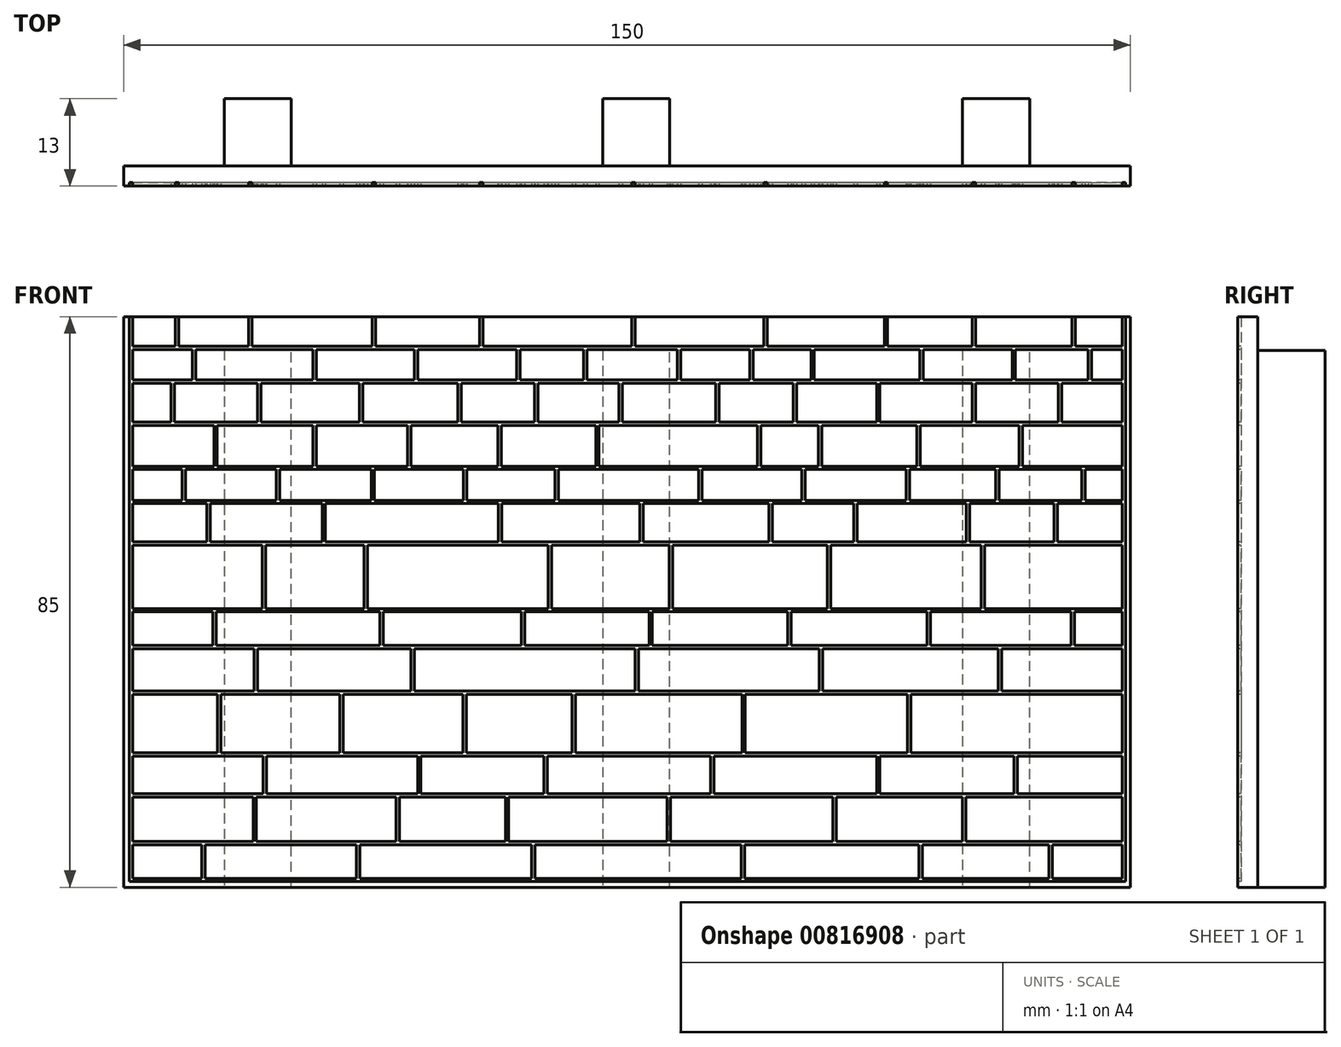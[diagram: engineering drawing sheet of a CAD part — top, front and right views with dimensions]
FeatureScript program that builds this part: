
annotation { "Feature Type Name" : "Feature", "Feature Type Description" : "" }
export const myFeature = defineFeature(function(context is Context, id is Id, definition is map)
    precondition{}
    {
        {
            var Q0;
            Q0=qCreatedBy(makeId("Front.planeOp"),FACE);
            var sketch = newSketch(context, id + "F0", { "sketchPlane" : qUnion([Q0])});
            skLineSegment(sketch, "E0.bottom", {"start": v(-65.97, 73.81) * mm, "end": v(-58.47, 73.81) * mm});
            skLineSegment(sketch, "E0.top", {"start": v(-65.97, -46.19) * mm, "end": v(84.03, -46.19) * mm});
            skLineSegment(sketch, "E0.left", {"start": v(-65.97, 73.81) * mm, "end": v(-65.97, -46.19) * mm});
            skLineSegment(sketch, "E0.right", {"start": v(84.03, 73.81) * mm, "end": v(84.03, -46.19) * mm});
            skLineSegment(sketch, "E1", {"start": v(-58.47, 73.81) * mm, "end": v(-58.47, 43.81) * mm});
            skLineSegment(sketch, "E2", {"start": v(-58.47, 43.81) * mm, "end": v(-43.47, 43.81) * mm});
            skLineSegment(sketch, "E3", {"start": v(-43.47, 43.81) * mm, "end": v(-43.47, 73.81) * mm});
            skLineSegment(sketch, "E4", {"start": v(-43.47, 73.81) * mm, "end": v(-28.47, 73.81) * mm});
            skLineSegment(sketch, "E5", {"start": v(1.53, 73.81) * mm, "end": v(1.53, 43.81) * mm});
            skLineSegment(sketch, "E6", {"start": v(1.53, 43.81) * mm, "end": v(16.53, 43.81) * mm});
            skLineSegment(sketch, "E7", {"start": v(16.53, 43.81) * mm, "end": v(16.53, 73.81) * mm});
            skLineSegment(sketch, "E8", {"start": v(16.53, 73.81) * mm, "end": v(31.53, 73.81) * mm});
            skLineSegment(sketch, "E9", {"start": v(61.53, 73.81) * mm, "end": v(61.53, 43.81) * mm});
            skLineSegment(sketch, "E10", {"start": v(61.53, 43.81) * mm, "end": v(76.53, 43.81) * mm});
            skLineSegment(sketch, "E11", {"start": v(76.53, 43.81) * mm, "end": v(76.53, 73.81) * mm});
            skLineSegment(sketch, "E12.trimOffspring", {"start": v(76.53, 73.81) * mm, "end": v(84.03, 73.81) * mm});
            skLineSegment(sketch, "E13", {"start": v(-28.47, 73.81) * mm, "end": v(-28.47, 43.81) * mm});
            skLineSegment(sketch, "E14", {"start": v(-28.47, 43.81) * mm, "end": v(-13.47, 43.81) * mm});
            skLineSegment(sketch, "E15", {"start": v(-13.47, 43.81) * mm, "end": v(-13.47, 73.81) * mm});
            skLineSegment(sketch, "E16", {"start": v(31.53, 73.81) * mm, "end": v(31.53, 43.81) * mm});
            skLineSegment(sketch, "E17", {"start": v(31.53, 43.81) * mm, "end": v(46.53, 43.81) * mm});
            skLineSegment(sketch, "E18", {"start": v(46.53, 43.81) * mm, "end": v(46.53, 73.81) * mm});
            skLineSegment(sketch, "E19.trimOffspring", {"start": v(-13.47, 73.81) * mm, "end": v(1.53, 73.81) * mm});
            skLineSegment(sketch, "E20.trimOffspring", {"start": v(46.53, 73.81) * mm, "end": v(61.53, 73.81) * mm});
            skSolve(sketch);
        }
        {
            var Q0;
            Q0=qSketchRegion(id+"F0",true);
            extrude(context, id + "F1", {"entities" : qUnion([Q0]), "depth" : 3 * mm, "offsetDistance" : 25 * mm});
        }
        {
            var Q0;
            Q0=makeQuery(id+"F1.opExtrude","CAP_FACE",FACE,{"disambiguationData":[OSD([sQuery(id+"F0.wireOp",EDGE,"E0.bottom"),sQuery(id+"F0.wireOp",EDGE,"E0.top"),sQuery(id+"F0.wireOp",EDGE,"E0.left"),sQuery(id+"F0.wireOp",EDGE,"E0.right"),sQuery(id+"F0.wireOp",EDGE,"E1"),sQuery(id+"F0.wireOp",EDGE,"E2"),sQuery(id+"F0.wireOp",EDGE,"E3"),sQuery(id+"F0.wireOp",EDGE,"E5"),sQuery(id+"F0.wireOp",EDGE,"E6"),sQuery(id+"F0.wireOp",EDGE,"E7"),sQuery(id+"F0.wireOp",EDGE,"E9"),sQuery(id+"F0.wireOp",EDGE,"E10"),sQuery(id+"F0.wireOp",EDGE,"E11"),sQuery(id+"F0.wireOp",EDGE,"E4"),sQuery(id+"F0.wireOp",EDGE,"E8"),sQuery(id+"F0.wireOp",EDGE,"E12.trimOffspring"),sQuery(id+"F0.wireOp",EDGE,"E13"),sQuery(id+"F0.wireOp",EDGE,"E14"),sQuery(id+"F0.wireOp",EDGE,"E15"),sQuery(id+"F0.wireOp",EDGE,"E16"),sQuery(id+"F0.wireOp",EDGE,"E17"),sQuery(id+"F0.wireOp",EDGE,"E18"),sQuery(id+"F0.wireOp",EDGE,"E19.trimOffspring"),sQuery(id+"F0.wireOp",EDGE,"E20.trimOffspring")])],"isStart":false});
            var sketch = newSketch(context, id + "F2", { "sketchPlane" : qUnion([Q0])});
            skLineSegment(sketch, "E21", {"start": v(-64.64, -39.38) * mm, "end": v(-46.68, -39.38) * mm});
            skLineSegment(sketch, "E22", {"start": v(83.31, -39.38) * mm, "end": v(83.31, -45.36) * mm});
            skLineSegment(sketch, "E23", {"start": v(83.31, -45.36) * mm, "end": v(-65.14, -45.36) * mm});
            skLineSegment(sketch, "E24", {"start": v(-65.14, -45.36) * mm, "end": v(-65.14, -39.38) * mm});
            skLineSegment(sketch, "E25.0", {"start": v(-64.64, -39.88) * mm, "end": v(-54.3, -39.88) * mm});
            skLineSegment(sketch, "E26.0", {"start": v(82.81, -44.86) * mm, "end": v(72.42, -44.86) * mm});
            skLineSegment(sketch, "E27.0", {"start": v(-64.64, -44.86) * mm, "end": v(-64.64, -39.88) * mm});
            skLineSegment(sketch, "E28.0", {"start": v(82.81, -39.88) * mm, "end": v(82.81, -44.86) * mm});
            skLineSegment(sketch, "E29", {"start": v(-65.14, -39.38) * mm, "end": v(-65.14, 34.42) * mm});
            skLineSegment(sketch, "E30", {"start": v(-64.64, 34.42) * mm, "end": v(-58.29, 34.42) * mm});
            skLineSegment(sketch, "E31", {"start": v(83.31, -39.38) * mm, "end": v(83.31, 34.42) * mm});
            skLineSegment(sketch, "E32.0", {"start": v(-64.64, -39.38) * mm, "end": v(-64.64, -32.73) * mm});
            skLineSegment(sketch, "E33.0", {"start": v(82.81, -39.38) * mm, "end": v(82.81, -32.73) * mm});
            skLineSegment(sketch, "E34", {"start": v(-64.64, -32.23) * mm, "end": v(-45.21, -32.23) * mm});
            skLineSegment(sketch, "E35", {"start": v(82.81, -26.17) * mm, "end": v(51.34, -26.17) * mm});
            skLineSegment(sketch, "E36", {"start": v(-64.64, -16.97) * mm, "end": v(-46.54, -16.97) * mm});
            skLineSegment(sketch, "E37", {"start": v(82.81, -10.62) * mm, "end": v(64.83, -10.62) * mm});
            skLineSegment(sketch, "E38", {"start": v(-64.64, -4.66) * mm, "end": v(-45.3, -4.66) * mm});
            skLineSegment(sketch, "E39", {"start": v(82.81, 4.76) * mm, "end": v(62.3, 4.76) * mm});
            skLineSegment(sketch, "E40", {"start": v(-64.64, 11.47) * mm, "end": v(-57.24, 11.47) * mm});
            skLineSegment(sketch, "E41", {"start": v(82.81, 16.05) * mm, "end": v(77.32, 16.05) * mm});
            skLineSegment(sketch, "E42", {"start": v(-64.64, 23.15) * mm, "end": v(-58.9, 23.15) * mm});
            skLineSegment(sketch, "E43", {"start": v(82.81, 28.92) * mm, "end": v(73.78, 28.92) * mm});
            skLineSegment(sketch, "E44.0", {"start": v(-64.64, -32.73) * mm, "end": v(-46.68, -32.73) * mm});
            skLineSegment(sketch, "E45.0", {"start": v(82.81, -26.67) * mm, "end": v(67.23, -26.67) * mm});
            skLineSegment(sketch, "E46.0", {"start": v(-64.64, -17.47) * mm, "end": v(-51.96, -17.47) * mm});
            skLineSegment(sketch, "E47.0", {"start": v(82.81, -10.12) * mm, "end": v(54.27, -10.12) * mm});
            skLineSegment(sketch, "E48.0", {"start": v(-64.64, -5.16) * mm, "end": v(-52.67, -5.16) * mm});
            skLineSegment(sketch, "E49.0", {"start": v(82.81, 5.26) * mm, "end": v(73.19, 5.26) * mm});
            skLineSegment(sketch, "E50.0", {"start": v(-64.64, 10.97) * mm, "end": v(10.98, 10.97) * mm});
            skLineSegment(sketch, "E51.0", {"start": v(82.81, 16.55) * mm, "end": v(67.98, 16.55) * mm});
            skLineSegment(sketch, "E52.0", {"start": v(-64.64, 22.65) * mm, "end": v(-52.52, 22.65) * mm});
            skLineSegment(sketch, "E53.0", {"start": v(82.81, 29.42) * mm, "end": v(78.25, 29.42) * mm});
            skLineSegment(sketch, "E54.0", {"start": v(-64.64, 33.92) * mm, "end": v(-55.72, 33.92) * mm});
            skLineSegment(sketch, "E55.trimOffspring", {"start": v(-64.64, 5.26) * mm, "end": v(-64.64, 10.97) * mm});
            skLineSegment(sketch, "E56.trimOffspring", {"start": v(-64.64, -4.66) * mm, "end": v(-64.64, 4.76) * mm});
            skLineSegment(sketch, "E57.trimOffspring", {"start": v(-64.64, -10.12) * mm, "end": v(-64.64, -5.16) * mm});
            skLineSegment(sketch, "E58.trimOffspring", {"start": v(-64.64, -16.97) * mm, "end": v(-64.64, -10.62) * mm});
            skLineSegment(sketch, "E59.trimOffspring", {"start": v(-64.64, -26.17) * mm, "end": v(-64.64, -17.47) * mm});
            skLineSegment(sketch, "E60.trimOffspring", {"start": v(-64.64, -32.23) * mm, "end": v(-64.64, -26.67) * mm});
            skLineSegment(sketch, "E61.trimOffspring", {"start": v(-64.64, 11.47) * mm, "end": v(-64.64, 16.05) * mm});
            skLineSegment(sketch, "E62.trimOffspring", {"start": v(-64.64, 16.55) * mm, "end": v(-64.64, 22.65) * mm});
            skLineSegment(sketch, "E63.trimOffspring", {"start": v(-64.64, 23.15) * mm, "end": v(-64.64, 28.92) * mm});
            skLineSegment(sketch, "E64.trimOffspring", {"start": v(-64.64, 29.42) * mm, "end": v(-64.64, 33.92) * mm});
            skLineSegment(sketch, "E65.trimOffspring", {"start": v(82.81, 29.42) * mm, "end": v(82.81, 33.92) * mm});
            skLineSegment(sketch, "E66.trimOffspring", {"start": v(82.81, 23.15) * mm, "end": v(82.81, 28.92) * mm});
            skLineSegment(sketch, "E67.trimOffspring", {"start": v(82.81, 16.55) * mm, "end": v(82.81, 22.65) * mm});
            skLineSegment(sketch, "E68.trimOffspring", {"start": v(82.81, 11.47) * mm, "end": v(82.81, 16.05) * mm});
            skLineSegment(sketch, "E69.trimOffspring", {"start": v(82.81, 5.26) * mm, "end": v(82.81, 10.97) * mm});
            skLineSegment(sketch, "E70.trimOffspring", {"start": v(82.81, -4.66) * mm, "end": v(82.81, 4.76) * mm});
            skLineSegment(sketch, "E71.trimOffspring", {"start": v(82.81, -10.12) * mm, "end": v(82.81, -5.16) * mm});
            skLineSegment(sketch, "E72.trimOffspring", {"start": v(82.81, -16.97) * mm, "end": v(82.81, -10.62) * mm});
            skLineSegment(sketch, "E73.trimOffspring", {"start": v(82.81, -26.17) * mm, "end": v(82.81, -17.47) * mm});
            skLineSegment(sketch, "E74.trimOffspring", {"start": v(82.81, -32.23) * mm, "end": v(82.81, -26.67) * mm});
            skLineSegment(sketch, "E75", {"start": v(-55.22, 33.92) * mm, "end": v(-55.22, 29.42) * mm});
            skLineSegment(sketch, "E76", {"start": v(-58.4, 28.92) * mm, "end": v(-58.4, 23.15) * mm});
            skLineSegment(sketch, "E77", {"start": v(-45.51, 28.92) * mm, "end": v(-45.51, 23.15) * mm});
            skLineSegment(sketch, "E78", {"start": v(-37.27, 33.92) * mm, "end": v(-37.27, 29.42) * mm});
            skLineSegment(sketch, "E79", {"start": v(-22.64, 29.42) * mm, "end": v(-22.64, 33.92) * mm});
            skLineSegment(sketch, "E80", {"start": v(-30.32, 28.92) * mm, "end": v(-30.32, 23.15) * mm});
            skLineSegment(sketch, "E81", {"start": v(-16.18, 23.15) * mm, "end": v(-16.18, 28.92) * mm});
            skLineSegment(sketch, "E82", {"start": v(-4.24, 28.92) * mm, "end": v(-4.24, 23.15) * mm});
            skLineSegment(sketch, "E83", {"start": v(-7.4, 29.42) * mm, "end": v(-7.4, 33.92) * mm});
            skLineSegment(sketch, "E84", {"start": v(2.56, 33.92) * mm, "end": v(2.56, 29.42) * mm});
            skLineSegment(sketch, "E85", {"start": v(8.34, 28.92) * mm, "end": v(8.34, 23.15) * mm});
            skLineSegment(sketch, "E86", {"start": v(16.52, 29.42) * mm, "end": v(16.52, 33.92) * mm});
            skLineSegment(sketch, "E87", {"start": v(27.82, 33.92) * mm, "end": v(27.82, 29.42) * mm});
            skLineSegment(sketch, "E88", {"start": v(22.75, 28.92) * mm, "end": v(22.75, 23.15) * mm});
            skLineSegment(sketch, "E89", {"start": v(36.45, 29.42) * mm, "end": v(36.45, 33.92) * mm});
            skLineSegment(sketch, "E90", {"start": v(34.32, 28.92) * mm, "end": v(34.32, 23.15) * mm});
            skLineSegment(sketch, "E91", {"start": v(46.22, 23.15) * mm, "end": v(46.22, 28.92) * mm});
            skLineSegment(sketch, "E92", {"start": v(52.64, 29.42) * mm, "end": v(52.64, 33.92) * mm});
            skLineSegment(sketch, "E93", {"start": v(61, 28.92) * mm, "end": v(61, 23.15) * mm});
            skLineSegment(sketch, "E94", {"start": v(73.28, 23.15) * mm, "end": v(73.28, 28.92) * mm});
            skLineSegment(sketch, "E95", {"start": v(66.42, 29.42) * mm, "end": v(66.42, 33.92) * mm});
            skLineSegment(sketch, "E96", {"start": v(78.25, 29.42) * mm, "end": v(78.25, 33.92) * mm});
            skLineSegment(sketch, "E97", {"start": v(67.98, 22.65) * mm, "end": v(67.98, 16.55) * mm});
            skLineSegment(sketch, "E98", {"start": v(52.73, 22.65) * mm, "end": v(52.73, 16.55) * mm});
            skLineSegment(sketch, "E99", {"start": v(38.05, 16.55) * mm, "end": v(38.05, 22.65) * mm});
            skLineSegment(sketch, "E100", {"start": v(28.98, 22.65) * mm, "end": v(28.98, 16.55) * mm});
            skLineSegment(sketch, "E101", {"start": v(4.38, 16.55) * mm, "end": v(4.38, 22.65) * mm});
            skLineSegment(sketch, "E102", {"start": v(-9.71, 22.65) * mm, "end": v(-9.71, 16.55) * mm});
            skLineSegment(sketch, "E103", {"start": v(-23.65, 16.55) * mm, "end": v(-23.65, 22.65) * mm});
            skLineSegment(sketch, "E104", {"start": v(-37.27, 22.65) * mm, "end": v(-37.27, 16.55) * mm});
            skLineSegment(sketch, "E105", {"start": v(-52.52, 16.55) * mm, "end": v(-52.52, 22.65) * mm});
            skLineSegment(sketch, "E106", {"start": v(-56.74, 16.05) * mm, "end": v(-56.74, 11.47) * mm});
            skLineSegment(sketch, "E107", {"start": v(-42.7, 16.05) * mm, "end": v(-42.7, 11.47) * mm});
            skLineSegment(sketch, "E108", {"start": v(-29.08, 11.47) * mm, "end": v(-29.08, 16.05) * mm});
            skLineSegment(sketch, "E109", {"start": v(-15.36, 11.47) * mm, "end": v(-15.36, 16.05) * mm});
            skLineSegment(sketch, "E110", {"start": v(-1.2, 16.05) * mm, "end": v(-1.2, 11.47) * mm});
            skLineSegment(sketch, "E111", {"start": v(19.7, 11.47) * mm, "end": v(19.7, 16.05) * mm});
            skLineSegment(sketch, "E112", {"start": v(35.6, 16.05) * mm, "end": v(35.6, 11.47) * mm});
            skLineSegment(sketch, "E113", {"start": v(51.12, 11.47) * mm, "end": v(51.12, 16.05) * mm});
            skLineSegment(sketch, "E114", {"start": v(64.48, 16.05) * mm, "end": v(64.48, 11.47) * mm});
            skLineSegment(sketch, "E115", {"start": v(77.32, 11.47) * mm, "end": v(77.32, 16.05) * mm});
            skLineSegment(sketch, "E116.0", {"start": v(35.1, 16.05) * mm, "end": v(35.1, 11.47) * mm});
            skLineSegment(sketch, "E117.0", {"start": v(50.62, 11.47) * mm, "end": v(50.62, 16.05) * mm});
            skLineSegment(sketch, "E118.0", {"start": v(63.98, 16.05) * mm, "end": v(63.98, 11.47) * mm});
            skLineSegment(sketch, "E119.0", {"start": v(76.82, 11.47) * mm, "end": v(76.82, 16.05) * mm});
            skLineSegment(sketch, "E120.0", {"start": v(67.48, 22.65) * mm, "end": v(67.48, 16.55) * mm});
            skLineSegment(sketch, "E121.0", {"start": v(52.23, 22.65) * mm, "end": v(52.23, 16.55) * mm});
            skLineSegment(sketch, "E122.0", {"start": v(37.55, 16.55) * mm, "end": v(37.55, 22.65) * mm});
            skLineSegment(sketch, "E123.0", {"start": v(28.48, 22.65) * mm, "end": v(28.48, 16.55) * mm});
            skLineSegment(sketch, "E124.0", {"start": v(20.2, 11.47) * mm, "end": v(20.2, 16.05) * mm});
            skLineSegment(sketch, "E125.0", {"start": v(-1.7, 16.05) * mm, "end": v(-1.7, 11.47) * mm});
            skLineSegment(sketch, "E126.0", {"start": v(4.88, 16.55) * mm, "end": v(4.88, 22.65) * mm});
            skLineSegment(sketch, "E127.0", {"start": v(-10.21, 22.65) * mm, "end": v(-10.21, 16.55) * mm});
            skLineSegment(sketch, "E128.0", {"start": v(-14.86, 11.47) * mm, "end": v(-14.86, 16.05) * mm});
            skLineSegment(sketch, "E129.0", {"start": v(-23.15, 16.55) * mm, "end": v(-23.15, 22.65) * mm});
            skLineSegment(sketch, "E130.0", {"start": v(-28.58, 11.47) * mm, "end": v(-28.58, 16.05) * mm});
            skLineSegment(sketch, "E131.0", {"start": v(-37.77, 22.65) * mm, "end": v(-37.77, 16.55) * mm});
            skLineSegment(sketch, "E132.0", {"start": v(-43.2, 16.05) * mm, "end": v(-43.2, 11.47) * mm});
            skLineSegment(sketch, "E133.0", {"start": v(-52.02, 16.55) * mm, "end": v(-52.02, 22.65) * mm});
            skLineSegment(sketch, "E134.0", {"start": v(-57.24, 16.05) * mm, "end": v(-57.24, 11.47) * mm});
            skLineSegment(sketch, "E135.0", {"start": v(-58.9, 28.92) * mm, "end": v(-58.9, 23.15) * mm});
            skLineSegment(sketch, "E136.0", {"start": v(-46.01, 28.92) * mm, "end": v(-46.01, 23.15) * mm});
            skLineSegment(sketch, "E137.0", {"start": v(-30.82, 28.92) * mm, "end": v(-30.82, 23.15) * mm});
            skLineSegment(sketch, "E138.0", {"start": v(-15.68, 23.15) * mm, "end": v(-15.68, 28.92) * mm});
            skLineSegment(sketch, "E139.0", {"start": v(-4.74, 28.92) * mm, "end": v(-4.74, 23.15) * mm});
            skLineSegment(sketch, "E140.0", {"start": v(7.84, 28.92) * mm, "end": v(7.84, 23.15) * mm});
            skLineSegment(sketch, "E141.0", {"start": v(22.25, 28.92) * mm, "end": v(22.25, 23.15) * mm});
            skLineSegment(sketch, "E142.0", {"start": v(33.82, 28.92) * mm, "end": v(33.82, 23.15) * mm});
            skLineSegment(sketch, "E143.0", {"start": v(46.72, 23.15) * mm, "end": v(46.72, 28.92) * mm});
            skLineSegment(sketch, "E144.0", {"start": v(60.5, 28.92) * mm, "end": v(60.5, 23.15) * mm});
            skLineSegment(sketch, "E145.0", {"start": v(73.78, 23.15) * mm, "end": v(73.78, 28.92) * mm});
            skLineSegment(sketch, "E146.0", {"start": v(77.75, 29.42) * mm, "end": v(77.75, 33.92) * mm});
            skLineSegment(sketch, "E147.0", {"start": v(66.92, 29.42) * mm, "end": v(66.92, 33.92) * mm});
            skLineSegment(sketch, "E148.0", {"start": v(53.14, 29.42) * mm, "end": v(53.14, 33.92) * mm});
            skLineSegment(sketch, "E149.0", {"start": v(36.95, 29.42) * mm, "end": v(36.95, 33.92) * mm});
            skLineSegment(sketch, "E150.0", {"start": v(27.32, 33.92) * mm, "end": v(27.32, 29.42) * mm});
            skLineSegment(sketch, "E151.0", {"start": v(17.02, 29.42) * mm, "end": v(17.02, 33.92) * mm});
            skLineSegment(sketch, "E152.0", {"start": v(3.06, 33.92) * mm, "end": v(3.06, 29.42) * mm});
            skLineSegment(sketch, "E153.0", {"start": v(-6.9, 29.42) * mm, "end": v(-6.9, 33.92) * mm});
            skLineSegment(sketch, "E154.0", {"start": v(-22.14, 29.42) * mm, "end": v(-22.14, 33.92) * mm});
            skLineSegment(sketch, "E155.0", {"start": v(-37.77, 33.92) * mm, "end": v(-37.77, 29.42) * mm});
            skLineSegment(sketch, "E156.0", {"start": v(-55.72, 33.92) * mm, "end": v(-55.72, 29.42) * mm});
            skLineSegment(sketch, "E157.trimOffspring", {"start": v(-55.72, 29.42) * mm, "end": v(-64.64, 29.42) * mm});
            skLineSegment(sketch, "E158.trimOffspring", {"start": v(-58.9, 28.92) * mm, "end": v(-64.64, 28.92) * mm});
            skLineSegment(sketch, "E159.trimOffspring", {"start": v(-46.01, 28.92) * mm, "end": v(-58.4, 28.92) * mm});
            skLineSegment(sketch, "E160.trimOffspring", {"start": v(-55.22, 33.92) * mm, "end": v(-37.77, 33.92) * mm});
            skLineSegment(sketch, "E161.trimOffspring", {"start": v(-37.27, 33.92) * mm, "end": v(-22.64, 33.92) * mm});
            skLineSegment(sketch, "E162.trimOffspring", {"start": v(-22.14, 33.92) * mm, "end": v(-7.4, 33.92) * mm});
            skLineSegment(sketch, "E163.trimOffspring", {"start": v(-30.82, 28.92) * mm, "end": v(-45.51, 28.92) * mm});
            skLineSegment(sketch, "E164.trimOffspring", {"start": v(-22.64, 29.42) * mm, "end": v(-55.22, 29.42) * mm});
            skLineSegment(sketch, "E165.trimOffspring", {"start": v(-16.18, 28.92) * mm, "end": v(-30.32, 28.92) * mm});
            skLineSegment(sketch, "E166.trimOffspring", {"start": v(-6.9, 33.92) * mm, "end": v(2.56, 33.92) * mm});
            skLineSegment(sketch, "E167.trimOffspring", {"start": v(-7.4, 29.42) * mm, "end": v(-22.14, 29.42) * mm});
            skLineSegment(sketch, "E168.trimOffspring", {"start": v(3.06, 33.92) * mm, "end": v(16.52, 33.92) * mm});
            skLineSegment(sketch, "E169.trimOffspring", {"start": v(2.56, 29.42) * mm, "end": v(-6.9, 29.42) * mm});
            skLineSegment(sketch, "E170.trimOffspring", {"start": v(-4.74, 28.92) * mm, "end": v(-15.68, 28.92) * mm});
            skLineSegment(sketch, "E171.trimOffspring", {"start": v(7.84, 28.92) * mm, "end": v(-4.24, 28.92) * mm});
            skLineSegment(sketch, "E172.trimOffspring", {"start": v(17.02, 33.92) * mm, "end": v(27.32, 33.92) * mm});
            skLineSegment(sketch, "E173.trimOffspring", {"start": v(16.52, 29.42) * mm, "end": v(3.06, 29.42) * mm});
            skLineSegment(sketch, "E174.trimOffspring", {"start": v(22.25, 28.92) * mm, "end": v(8.34, 28.92) * mm});
            skLineSegment(sketch, "E175.trimOffspring", {"start": v(27.32, 29.42) * mm, "end": v(17.02, 29.42) * mm});
            skLineSegment(sketch, "E176.trimOffspring", {"start": v(27.82, 33.92) * mm, "end": v(36.45, 33.92) * mm});
            skLineSegment(sketch, "E177.trimOffspring", {"start": v(36.95, 33.92) * mm, "end": v(52.64, 33.92) * mm});
            skLineSegment(sketch, "E178.trimOffspring", {"start": v(36.45, 29.42) * mm, "end": v(27.82, 29.42) * mm});
            skLineSegment(sketch, "E179.trimOffspring", {"start": v(33.82, 28.92) * mm, "end": v(22.75, 28.92) * mm});
            skLineSegment(sketch, "E180.trimOffspring", {"start": v(53.14, 33.92) * mm, "end": v(66.42, 33.92) * mm});
            skLineSegment(sketch, "E181.trimOffspring", {"start": v(52.64, 29.42) * mm, "end": v(36.95, 29.42) * mm});
            skLineSegment(sketch, "E182.trimOffspring", {"start": v(46.22, 28.92) * mm, "end": v(34.32, 28.92) * mm});
            skLineSegment(sketch, "E183.trimOffspring", {"start": v(60.5, 28.92) * mm, "end": v(46.72, 28.92) * mm});
            skLineSegment(sketch, "E184.trimOffspring", {"start": v(66.42, 29.42) * mm, "end": v(53.14, 29.42) * mm});
            skLineSegment(sketch, "E185.trimOffspring", {"start": v(66.92, 33.92) * mm, "end": v(77.75, 33.92) * mm});
            skLineSegment(sketch, "E186.trimOffspring", {"start": v(73.28, 28.92) * mm, "end": v(61, 28.92) * mm});
            skLineSegment(sketch, "E187.trimOffspring", {"start": v(77.75, 29.42) * mm, "end": v(66.92, 29.42) * mm});
            skLineSegment(sketch, "E188.trimOffspring", {"start": v(78.25, 33.92) * mm, "end": v(82.81, 33.92) * mm});
            skLineSegment(sketch, "E189.trimOffspring", {"start": v(73.78, 23.15) * mm, "end": v(82.81, 23.15) * mm});
            skLineSegment(sketch, "E190.trimOffspring", {"start": v(67.98, 22.65) * mm, "end": v(82.81, 22.65) * mm});
            skLineSegment(sketch, "E191.trimOffspring", {"start": v(61, 23.15) * mm, "end": v(73.28, 23.15) * mm});
            skLineSegment(sketch, "E192.trimOffspring", {"start": v(52.73, 22.65) * mm, "end": v(67.48, 22.65) * mm});
            skLineSegment(sketch, "E193.trimOffspring", {"start": v(46.72, 23.15) * mm, "end": v(60.5, 23.15) * mm});
            skLineSegment(sketch, "E194.trimOffspring", {"start": v(38.05, 22.65) * mm, "end": v(52.23, 22.65) * mm});
            skLineSegment(sketch, "E195.trimOffspring", {"start": v(34.32, 23.15) * mm, "end": v(46.22, 23.15) * mm});
            skLineSegment(sketch, "E196.trimOffspring", {"start": v(28.98, 22.65) * mm, "end": v(37.55, 22.65) * mm});
            skLineSegment(sketch, "E197.trimOffspring", {"start": v(22.75, 23.15) * mm, "end": v(33.82, 23.15) * mm});
            skLineSegment(sketch, "E198.trimOffspring", {"start": v(8.34, 23.15) * mm, "end": v(22.25, 23.15) * mm});
            skLineSegment(sketch, "E199.trimOffspring", {"start": v(4.88, 22.65) * mm, "end": v(28.48, 22.65) * mm});
            skLineSegment(sketch, "E200.trimOffspring", {"start": v(-4.24, 23.15) * mm, "end": v(7.84, 23.15) * mm});
            skLineSegment(sketch, "E201.trimOffspring", {"start": v(-15.68, 23.15) * mm, "end": v(-4.74, 23.15) * mm});
            skLineSegment(sketch, "E202.trimOffspring", {"start": v(-23.15, 22.65) * mm, "end": v(4.38, 22.65) * mm});
            skLineSegment(sketch, "E203.trimOffspring", {"start": v(-30.32, 23.15) * mm, "end": v(-16.18, 23.15) * mm});
            skLineSegment(sketch, "E204.trimOffspring", {"start": v(-37.27, 22.65) * mm, "end": v(-23.65, 22.65) * mm});
            skLineSegment(sketch, "E205.trimOffspring", {"start": v(-45.51, 23.15) * mm, "end": v(-30.82, 23.15) * mm});
            skLineSegment(sketch, "E206.trimOffspring", {"start": v(-52.02, 22.65) * mm, "end": v(-37.77, 22.65) * mm});
            skLineSegment(sketch, "E207.trimOffspring", {"start": v(-58.4, 23.15) * mm, "end": v(-46.01, 23.15) * mm});
            skLineSegment(sketch, "E208.trimOffspring", {"start": v(-57.24, 16.05) * mm, "end": v(-64.64, 16.05) * mm});
            skLineSegment(sketch, "E209.trimOffspring", {"start": v(-52.52, 16.55) * mm, "end": v(-64.64, 16.55) * mm});
            skLineSegment(sketch, "E210.trimOffspring", {"start": v(-43.2, 16.05) * mm, "end": v(-56.74, 16.05) * mm});
            skLineSegment(sketch, "E211.trimOffspring", {"start": v(-37.77, 16.55) * mm, "end": v(-52.02, 16.55) * mm});
            skLineSegment(sketch, "E212.trimOffspring", {"start": v(-29.08, 16.05) * mm, "end": v(-42.7, 16.05) * mm});
            skLineSegment(sketch, "E213.trimOffspring", {"start": v(-23.65, 16.55) * mm, "end": v(-37.27, 16.55) * mm});
            skLineSegment(sketch, "E214.trimOffspring", {"start": v(-15.36, 16.05) * mm, "end": v(-28.58, 16.05) * mm});
            skLineSegment(sketch, "E215.trimOffspring", {"start": v(-10.21, 16.55) * mm, "end": v(-23.15, 16.55) * mm});
            skLineSegment(sketch, "E216.trimOffspring", {"start": v(-1.7, 16.05) * mm, "end": v(-14.86, 16.05) * mm});
            skLineSegment(sketch, "E217.trimOffspring", {"start": v(4.38, 16.55) * mm, "end": v(-9.71, 16.55) * mm});
            skLineSegment(sketch, "E218.trimOffspring", {"start": v(19.7, 16.05) * mm, "end": v(-1.2, 16.05) * mm});
            skLineSegment(sketch, "E219.trimOffspring", {"start": v(28.48, 16.55) * mm, "end": v(4.88, 16.55) * mm});
            skLineSegment(sketch, "E220.trimOffspring", {"start": v(35.1, 16.05) * mm, "end": v(20.2, 16.05) * mm});
            skLineSegment(sketch, "E221.trimOffspring", {"start": v(37.55, 16.55) * mm, "end": v(28.98, 16.55) * mm});
            skLineSegment(sketch, "E222.trimOffspring", {"start": v(50.62, 16.05) * mm, "end": v(35.6, 16.05) * mm});
            skLineSegment(sketch, "E223.trimOffspring", {"start": v(52.23, 16.55) * mm, "end": v(38.05, 16.55) * mm});
            skLineSegment(sketch, "E224.trimOffspring", {"start": v(63.98, 16.05) * mm, "end": v(51.12, 16.05) * mm});
            skLineSegment(sketch, "E225.trimOffspring", {"start": v(67.48, 16.55) * mm, "end": v(52.73, 16.55) * mm});
            skLineSegment(sketch, "E226.trimOffspring", {"start": v(76.82, 16.05) * mm, "end": v(64.48, 16.05) * mm});
            skLineSegment(sketch, "E227.trimOffspring", {"start": v(77.32, 11.47) * mm, "end": v(82.81, 11.47) * mm});
            skLineSegment(sketch, "E228.trimOffspring", {"start": v(64.48, 11.47) * mm, "end": v(76.82, 11.47) * mm});
            skLineSegment(sketch, "E229.trimOffspring", {"start": v(51.12, 11.47) * mm, "end": v(63.98, 11.47) * mm});
            skLineSegment(sketch, "E230.trimOffspring", {"start": v(35.6, 11.47) * mm, "end": v(50.62, 11.47) * mm});
            skLineSegment(sketch, "E231.trimOffspring", {"start": v(20.2, 11.47) * mm, "end": v(35.1, 11.47) * mm});
            skLineSegment(sketch, "E232.trimOffspring", {"start": v(-1.2, 11.47) * mm, "end": v(19.7, 11.47) * mm});
            skLineSegment(sketch, "E233.trimOffspring", {"start": v(-14.86, 11.47) * mm, "end": v(-1.7, 11.47) * mm});
            skLineSegment(sketch, "E234.trimOffspring", {"start": v(-28.58, 11.47) * mm, "end": v(-15.36, 11.47) * mm});
            skLineSegment(sketch, "E235.trimOffspring", {"start": v(-42.7, 11.47) * mm, "end": v(-29.08, 11.47) * mm});
            skLineSegment(sketch, "E236.trimOffspring", {"start": v(-56.74, 11.47) * mm, "end": v(-43.2, 11.47) * mm});
            skLineSegment(sketch, "E237", {"start": v(-53.08, 10.97) * mm, "end": v(-53.08, 5.26) * mm});
            skLineSegment(sketch, "E238", {"start": v(-35.9, 10.97) * mm, "end": v(-35.9, 5.26) * mm});
            skLineSegment(sketch, "E239", {"start": v(-9.64, 10.97) * mm, "end": v(-9.64, 5.26) * mm});
            skLineSegment(sketch, "E240", {"start": v(11.48, 10.97) * mm, "end": v(11.48, 5.26) * mm});
            skLineSegment(sketch, "E241", {"start": v(30.2, 5.26) * mm, "end": v(30.2, 10.97) * mm});
            skLineSegment(sketch, "E242", {"start": v(43.35, 10.97) * mm, "end": v(43.35, 5.26) * mm});
            skLineSegment(sketch, "E243", {"start": v(60.08, 10.97) * mm, "end": v(60.08, 5.26) * mm});
            skLineSegment(sketch, "E244", {"start": v(72.69, 5.26) * mm, "end": v(72.69, 10.97) * mm});
            skLineSegment(sketch, "E245", {"start": v(62.3, 4.76) * mm, "end": v(62.3, -4.66) * mm});
            skLineSegment(sketch, "E246", {"start": v(39.4, 4.76) * mm, "end": v(39.4, -4.66) * mm});
            skLineSegment(sketch, "E247", {"start": v(15.34, 4.76) * mm, "end": v(15.34, -4.66) * mm});
            skLineSegment(sketch, "E248", {"start": v(-2.2, 4.76) * mm, "end": v(-2.2, -4.66) * mm});
            skLineSegment(sketch, "E249", {"start": v(-29.62, 4.76) * mm, "end": v(-29.62, -4.66) * mm});
            skLineSegment(sketch, "E250", {"start": v(-44.8, 4.76) * mm, "end": v(-44.8, -4.66) * mm});
            skLineSegment(sketch, "E251", {"start": v(-52.17, -5.16) * mm, "end": v(-52.17, -10.12) * mm});
            skLineSegment(sketch, "E252", {"start": v(-27.27, -5.16) * mm, "end": v(-27.27, -10.12) * mm});
            skLineSegment(sketch, "E253", {"start": v(-6.19, -5.16) * mm, "end": v(-6.19, -10.12) * mm});
            skLineSegment(sketch, "E254", {"start": v(12.81, -5.16) * mm, "end": v(12.81, -10.12) * mm});
            skLineSegment(sketch, "E255", {"start": v(32.96, -10.12) * mm, "end": v(32.96, -5.16) * mm});
            skLineSegment(sketch, "E256", {"start": v(54.27, -5.16) * mm, "end": v(54.27, -10.12) * mm});
            skLineSegment(sketch, "E257", {"start": v(75.22, -10.12) * mm, "end": v(75.22, -5.16) * mm});
            skLineSegment(sketch, "E258", {"start": v(64.83, -10.62) * mm, "end": v(64.83, -16.97) * mm});
            skLineSegment(sketch, "E259", {"start": v(51.34, -17.47) * mm, "end": v(51.34, -26.17) * mm});
            skLineSegment(sketch, "E260", {"start": v(37.67, -16.97) * mm, "end": v(37.67, -10.62) * mm});
            skLineSegment(sketch, "E261", {"start": v(26.66, -17.47) * mm, "end": v(26.66, -26.17) * mm});
            skLineSegment(sketch, "E262", {"start": v(1.36, -26.17) * mm, "end": v(1.36, -17.47) * mm});
            skLineSegment(sketch, "E263", {"start": v(10.24, -16.97) * mm, "end": v(10.24, -10.62) * mm});
            skLineSegment(sketch, "E264", {"start": v(-14.88, -17.47) * mm, "end": v(-14.88, -26.17) * mm});
            skLineSegment(sketch, "E265", {"start": v(-23.14, -16.97) * mm, "end": v(-23.14, -10.62) * mm});
            skLineSegment(sketch, "E266", {"start": v(-46.04, -10.62) * mm, "end": v(-46.04, -16.97) * mm});
            skLineSegment(sketch, "E267", {"start": v(-51.46, -17.47) * mm, "end": v(-51.46, -26.17) * mm});
            skLineSegment(sketch, "E268", {"start": v(-33.26, -17.47) * mm, "end": v(-33.26, -26.17) * mm});
            skLineSegment(sketch, "E269", {"start": v(-44.71, -26.67) * mm, "end": v(-44.71, -32.23) * mm});
            skLineSegment(sketch, "E270", {"start": v(-22.16, -32.23) * mm, "end": v(-22.16, -26.67) * mm});
            skLineSegment(sketch, "E271", {"start": v(-2.81, -26.67) * mm, "end": v(-2.81, -32.23) * mm});
            skLineSegment(sketch, "E272", {"start": v(21.51, -32.23) * mm, "end": v(21.51, -26.67) * mm});
            skLineSegment(sketch, "E273", {"start": v(46.72, -26.67) * mm, "end": v(46.72, -32.23) * mm});
            skLineSegment(sketch, "E274", {"start": v(67.23, -26.67) * mm, "end": v(67.23, -32.23) * mm});
            skLineSegment(sketch, "E275", {"start": v(59.5, -32.73) * mm, "end": v(59.5, -39.38) * mm});
            skLineSegment(sketch, "E276", {"start": v(39.7, -39.38) * mm, "end": v(39.7, -32.73) * mm});
            skLineSegment(sketch, "E277", {"start": v(15.03, -39.38) * mm, "end": v(15.03, -32.73) * mm});
            skLineSegment(sketch, "E278", {"start": v(-8.58, -32.73) * mm, "end": v(-8.58, -39.38) * mm});
            skLineSegment(sketch, "E279", {"start": v(-30.77, -39.88) * mm, "end": v(-30.77, -44.86) * mm});
            skLineSegment(sketch, "E280", {"start": v(-25.36, -39.38) * mm, "end": v(-25.36, -32.73) * mm});
            skLineSegment(sketch, "E281", {"start": v(-46.18, -32.73) * mm, "end": v(-46.18, -39.38) * mm});
            skLineSegment(sketch, "E282", {"start": v(-53.8, -39.88) * mm, "end": v(-53.8, -44.86) * mm});
            skLineSegment(sketch, "E283", {"start": v(-5.16, -44.86) * mm, "end": v(-5.16, -39.88) * mm});
            skLineSegment(sketch, "E284", {"start": v(26.08, -44.86) * mm, "end": v(26.08, -39.88) * mm});
            skLineSegment(sketch, "E285", {"start": v(52.53, -44.86) * mm, "end": v(52.53, -39.88) * mm});
            skLineSegment(sketch, "E286", {"start": v(72.42, -39.88) * mm, "end": v(72.42, -44.86) * mm});
            skLineSegment(sketch, "E287.0", {"start": v(-53.58, 10.97) * mm, "end": v(-53.58, 5.26) * mm});
            skLineSegment(sketch, "E288.0", {"start": v(-36.4, 10.97) * mm, "end": v(-36.4, 5.26) * mm});
            skLineSegment(sketch, "E289.0", {"start": v(-10.14, 10.97) * mm, "end": v(-10.14, 5.26) * mm});
            skLineSegment(sketch, "E290.0", {"start": v(-2.7, 4.76) * mm, "end": v(-2.7, -4.66) * mm});
            skLineSegment(sketch, "E291.0", {"start": v(-30.12, 4.76) * mm, "end": v(-30.12, -4.66) * mm});
            skLineSegment(sketch, "E292.0", {"start": v(-45.3, 4.76) * mm, "end": v(-45.3, -4.66) * mm});
            skLineSegment(sketch, "E293.0", {"start": v(-52.67, -5.16) * mm, "end": v(-52.67, -10.12) * mm});
            skLineSegment(sketch, "E294.0", {"start": v(-27.77, -5.16) * mm, "end": v(-27.77, -10.12) * mm});
            skLineSegment(sketch, "E295.0", {"start": v(-6.69, -5.16) * mm, "end": v(-6.69, -10.12) * mm});
            skLineSegment(sketch, "E296.0", {"start": v(10.98, 10.97) * mm, "end": v(10.98, 5.26) * mm});
            skLineSegment(sketch, "E297.0", {"start": v(30.7, 5.26) * mm, "end": v(30.7, 10.97) * mm});
            skLineSegment(sketch, "E298.0", {"start": v(42.85, 10.97) * mm, "end": v(42.85, 5.26) * mm});
            skLineSegment(sketch, "E299.0", {"start": v(59.58, 10.97) * mm, "end": v(59.58, 5.26) * mm});
            skLineSegment(sketch, "E300.0", {"start": v(73.19, 5.26) * mm, "end": v(73.19, 10.97) * mm});
            skLineSegment(sketch, "E301.0", {"start": v(61.8, 4.76) * mm, "end": v(61.8, -4.66) * mm});
            skLineSegment(sketch, "E302.0", {"start": v(75.72, -10.12) * mm, "end": v(75.72, -5.16) * mm});
            skLineSegment(sketch, "E303.0", {"start": v(53.77, -5.16) * mm, "end": v(53.77, -10.12) * mm});
            skLineSegment(sketch, "E304.0", {"start": v(38.9, 4.76) * mm, "end": v(38.9, -4.66) * mm});
            skLineSegment(sketch, "E305.0", {"start": v(15.84, 4.76) * mm, "end": v(15.84, -4.66) * mm});
            skLineSegment(sketch, "E306.0", {"start": v(12.31, -5.16) * mm, "end": v(12.31, -10.12) * mm});
            skLineSegment(sketch, "E307.0", {"start": v(33.46, -10.12) * mm, "end": v(33.46, -5.16) * mm});
            skLineSegment(sketch, "E308.0", {"start": v(64.33, -10.62) * mm, "end": v(64.33, -16.97) * mm});
            skLineSegment(sketch, "E309.0", {"start": v(38.17, -16.97) * mm, "end": v(38.17, -10.62) * mm});
            skLineSegment(sketch, "E310.0", {"start": v(10.74, -16.97) * mm, "end": v(10.74, -10.62) * mm});
            skLineSegment(sketch, "E311.0", {"start": v(0.86, -26.17) * mm, "end": v(0.86, -17.47) * mm});
            skLineSegment(sketch, "E312.0", {"start": v(26.16, -17.47) * mm, "end": v(26.16, -26.17) * mm});
            skLineSegment(sketch, "E313.0", {"start": v(50.84, -17.47) * mm, "end": v(50.84, -26.17) * mm});
            skLineSegment(sketch, "E314.0", {"start": v(66.73, -26.67) * mm, "end": v(66.73, -32.23) * mm});
            skLineSegment(sketch, "E315.0", {"start": v(46.22, -26.67) * mm, "end": v(46.22, -32.23) * mm});
            skLineSegment(sketch, "E316.0", {"start": v(22.01, -32.23) * mm, "end": v(22.01, -26.67) * mm});
            skLineSegment(sketch, "E317.0", {"start": v(15.53, -39.38) * mm, "end": v(15.53, -32.73) * mm});
            skLineSegment(sketch, "E318.0", {"start": v(40.2, -39.38) * mm, "end": v(40.2, -32.73) * mm});
            skLineSegment(sketch, "E319.0", {"start": v(59, -32.73) * mm, "end": v(59, -39.38) * mm});
            skLineSegment(sketch, "E320.0", {"start": v(71.92, -39.88) * mm, "end": v(71.92, -44.86) * mm});
            skLineSegment(sketch, "E321.0", {"start": v(53.03, -44.86) * mm, "end": v(53.03, -39.88) * mm});
            skLineSegment(sketch, "E322.0", {"start": v(26.58, -44.86) * mm, "end": v(26.58, -39.88) * mm});
            skLineSegment(sketch, "E323.0", {"start": v(-4.66, -44.86) * mm, "end": v(-4.66, -39.88) * mm});
            skLineSegment(sketch, "E324.0", {"start": v(-9.08, -32.73) * mm, "end": v(-9.08, -39.38) * mm});
            skLineSegment(sketch, "E325.0", {"start": v(-3.31, -26.67) * mm, "end": v(-3.31, -32.23) * mm});
            skLineSegment(sketch, "E326.0", {"start": v(-15.38, -17.47) * mm, "end": v(-15.38, -26.17) * mm});
            skLineSegment(sketch, "E327.0", {"start": v(-22.64, -16.97) * mm, "end": v(-22.64, -10.62) * mm});
            skLineSegment(sketch, "E328.0", {"start": v(-46.54, -10.62) * mm, "end": v(-46.54, -16.97) * mm});
            skLineSegment(sketch, "E329.0", {"start": v(-51.96, -17.47) * mm, "end": v(-51.96, -26.17) * mm});
            skLineSegment(sketch, "E330.0", {"start": v(-33.76, -17.47) * mm, "end": v(-33.76, -26.17) * mm});
            skLineSegment(sketch, "E331.0", {"start": v(-45.21, -26.67) * mm, "end": v(-45.21, -32.23) * mm});
            skLineSegment(sketch, "E332.0", {"start": v(-21.66, -32.23) * mm, "end": v(-21.66, -26.67) * mm});
            skLineSegment(sketch, "E333.0", {"start": v(-24.86, -39.38) * mm, "end": v(-24.86, -32.73) * mm});
            skLineSegment(sketch, "E334.0", {"start": v(-46.68, -32.73) * mm, "end": v(-46.68, -39.38) * mm});
            skLineSegment(sketch, "E335.0", {"start": v(-54.3, -39.88) * mm, "end": v(-54.3, -44.86) * mm});
            skLineSegment(sketch, "E336.0", {"start": v(-31.27, -39.88) * mm, "end": v(-31.27, -44.86) * mm});
            skLineSegment(sketch, "E337.trimOffspring", {"start": v(-53.58, 5.26) * mm, "end": v(-64.64, 5.26) * mm});
            skLineSegment(sketch, "E338.trimOffspring", {"start": v(-36.4, 5.26) * mm, "end": v(-53.08, 5.26) * mm});
            skLineSegment(sketch, "E339.trimOffspring", {"start": v(-45.3, 4.76) * mm, "end": v(-64.64, 4.76) * mm});
            skLineSegment(sketch, "E340.trimOffspring", {"start": v(-30.12, 4.76) * mm, "end": v(-44.8, 4.76) * mm});
            skLineSegment(sketch, "E341.trimOffspring", {"start": v(-2.7, 4.76) * mm, "end": v(-29.62, 4.76) * mm});
            skLineSegment(sketch, "E342.trimOffspring", {"start": v(-10.14, 5.26) * mm, "end": v(-35.9, 5.26) * mm});
            skLineSegment(sketch, "E343.trimOffspring", {"start": v(10.98, 5.26) * mm, "end": v(-9.64, 5.26) * mm});
            skLineSegment(sketch, "E344.trimOffspring", {"start": v(15.34, 4.76) * mm, "end": v(-2.2, 4.76) * mm});
            skLineSegment(sketch, "E345.trimOffspring", {"start": v(38.9, 4.76) * mm, "end": v(15.84, 4.76) * mm});
            skLineSegment(sketch, "E346.trimOffspring", {"start": v(42.85, 5.26) * mm, "end": v(30.7, 5.26) * mm});
            skLineSegment(sketch, "E347.trimOffspring", {"start": v(59.58, 5.26) * mm, "end": v(43.35, 5.26) * mm});
            skLineSegment(sketch, "E348.trimOffspring", {"start": v(61.8, 4.76) * mm, "end": v(39.4, 4.76) * mm});
            skLineSegment(sketch, "E349.trimOffspring", {"start": v(72.69, 5.26) * mm, "end": v(60.08, 5.26) * mm});
            skLineSegment(sketch, "E350.trimOffspring", {"start": v(75.72, -5.16) * mm, "end": v(82.81, -5.16) * mm});
            skLineSegment(sketch, "E351.trimOffspring", {"start": v(62.3, -4.66) * mm, "end": v(82.81, -4.66) * mm});
            skLineSegment(sketch, "E352.trimOffspring", {"start": v(64.33, -10.62) * mm, "end": v(38.17, -10.62) * mm});
            skLineSegment(sketch, "E353.trimOffspring", {"start": v(53.77, -10.12) * mm, "end": v(33.46, -10.12) * mm});
            skLineSegment(sketch, "E354.trimOffspring", {"start": v(54.27, -5.16) * mm, "end": v(75.22, -5.16) * mm});
            skLineSegment(sketch, "E355.trimOffspring", {"start": v(39.4, -4.66) * mm, "end": v(61.8, -4.66) * mm});
            skLineSegment(sketch, "E356.trimOffspring", {"start": v(33.46, -5.16) * mm, "end": v(53.77, -5.16) * mm});
            skLineSegment(sketch, "E357.trimOffspring", {"start": v(37.67, -10.62) * mm, "end": v(10.74, -10.62) * mm});
            skLineSegment(sketch, "E358.trimOffspring", {"start": v(32.96, -10.12) * mm, "end": v(12.81, -10.12) * mm});
            skLineSegment(sketch, "E359.trimOffspring", {"start": v(15.84, -4.66) * mm, "end": v(38.9, -4.66) * mm});
            skLineSegment(sketch, "E360.trimOffspring", {"start": v(12.81, -5.16) * mm, "end": v(32.96, -5.16) * mm});
            skLineSegment(sketch, "E361.trimOffspring", {"start": v(12.31, -10.12) * mm, "end": v(-6.19, -10.12) * mm});
            skLineSegment(sketch, "E362.trimOffspring", {"start": v(10.24, -10.62) * mm, "end": v(-22.64, -10.62) * mm});
            skLineSegment(sketch, "E363.trimOffspring", {"start": v(-2.2, -4.66) * mm, "end": v(15.34, -4.66) * mm});
            skLineSegment(sketch, "E364.trimOffspring", {"start": v(-6.19, -5.16) * mm, "end": v(12.31, -5.16) * mm});
            skLineSegment(sketch, "E365.trimOffspring", {"start": v(-6.69, -10.12) * mm, "end": v(-27.27, -10.12) * mm});
            skLineSegment(sketch, "E366.trimOffspring", {"start": v(-23.14, -10.62) * mm, "end": v(-46.04, -10.62) * mm});
            skLineSegment(sketch, "E367.trimOffspring", {"start": v(-27.77, -10.12) * mm, "end": v(-52.17, -10.12) * mm});
            skLineSegment(sketch, "E368.trimOffspring", {"start": v(-27.27, -5.16) * mm, "end": v(-6.69, -5.16) * mm});
            skLineSegment(sketch, "E369.trimOffspring", {"start": v(-29.62, -4.66) * mm, "end": v(-2.7, -4.66) * mm});
            skLineSegment(sketch, "E370.trimOffspring", {"start": v(-44.8, -4.66) * mm, "end": v(-30.12, -4.66) * mm});
            skLineSegment(sketch, "E371.trimOffspring", {"start": v(-52.17, -5.16) * mm, "end": v(-27.77, -5.16) * mm});
            skLineSegment(sketch, "E372.trimOffspring", {"start": v(-52.67, -10.12) * mm, "end": v(-64.64, -10.12) * mm});
            skLineSegment(sketch, "E373.trimOffspring", {"start": v(-46.54, -10.62) * mm, "end": v(-64.64, -10.62) * mm});
            skLineSegment(sketch, "E374.trimOffspring", {"start": v(-51.46, -17.47) * mm, "end": v(-33.76, -17.47) * mm});
            skLineSegment(sketch, "E375.trimOffspring", {"start": v(-46.04, -16.97) * mm, "end": v(-23.14, -16.97) * mm});
            skLineSegment(sketch, "E376.trimOffspring", {"start": v(-45.21, -26.67) * mm, "end": v(-64.64, -26.67) * mm});
            skLineSegment(sketch, "E377.trimOffspring", {"start": v(-33.76, -26.17) * mm, "end": v(-64.64, -26.17) * mm});
            skLineSegment(sketch, "E378.trimOffspring", {"start": v(-33.26, -17.47) * mm, "end": v(-15.38, -17.47) * mm});
            skLineSegment(sketch, "E379.trimOffspring", {"start": v(-22.64, -16.97) * mm, "end": v(10.24, -16.97) * mm});
            skLineSegment(sketch, "E380.trimOffspring", {"start": v(-22.16, -26.67) * mm, "end": v(-44.71, -26.67) * mm});
            skLineSegment(sketch, "E381.trimOffspring", {"start": v(-15.38, -26.17) * mm, "end": v(-33.26, -26.17) * mm});
            skLineSegment(sketch, "E382.trimOffspring", {"start": v(-14.88, -17.47) * mm, "end": v(0.86, -17.47) * mm});
            skLineSegment(sketch, "E383.trimOffspring", {"start": v(-3.31, -26.67) * mm, "end": v(-21.66, -26.67) * mm});
            skLineSegment(sketch, "E384.trimOffspring", {"start": v(0.86, -26.17) * mm, "end": v(-14.88, -26.17) * mm});
            skLineSegment(sketch, "E385.trimOffspring", {"start": v(1.36, -17.47) * mm, "end": v(26.16, -17.47) * mm});
            skLineSegment(sketch, "E386.trimOffspring", {"start": v(10.74, -16.97) * mm, "end": v(37.67, -16.97) * mm});
            skLineSegment(sketch, "E387.trimOffspring", {"start": v(21.51, -26.67) * mm, "end": v(-2.81, -26.67) * mm});
            skLineSegment(sketch, "E388.trimOffspring", {"start": v(26.16, -26.17) * mm, "end": v(1.36, -26.17) * mm});
            skLineSegment(sketch, "E389.trimOffspring", {"start": v(26.66, -17.47) * mm, "end": v(50.84, -17.47) * mm});
            skLineSegment(sketch, "E390.trimOffspring", {"start": v(38.17, -16.97) * mm, "end": v(64.33, -16.97) * mm});
            skLineSegment(sketch, "E391.trimOffspring", {"start": v(51.34, -17.47) * mm, "end": v(82.81, -17.47) * mm});
            skLineSegment(sketch, "E392.trimOffspring", {"start": v(50.84, -26.17) * mm, "end": v(26.66, -26.17) * mm});
            skLineSegment(sketch, "E393.trimOffspring", {"start": v(46.22, -26.67) * mm, "end": v(22.01, -26.67) * mm});
            skLineSegment(sketch, "E394.trimOffspring", {"start": v(64.83, -16.97) * mm, "end": v(82.81, -16.97) * mm});
            skLineSegment(sketch, "E395.trimOffspring", {"start": v(66.73, -26.67) * mm, "end": v(46.72, -26.67) * mm});
            skLineSegment(sketch, "E396.trimOffspring", {"start": v(67.23, -32.23) * mm, "end": v(82.81, -32.23) * mm});
            skLineSegment(sketch, "E397.trimOffspring", {"start": v(59.5, -32.73) * mm, "end": v(82.81, -32.73) * mm});
            skLineSegment(sketch, "E398.trimOffspring", {"start": v(59.5, -39.38) * mm, "end": v(82.81, -39.38) * mm});
            skLineSegment(sketch, "E399.trimOffspring", {"start": v(46.72, -32.23) * mm, "end": v(66.73, -32.23) * mm});
            skLineSegment(sketch, "E400.trimOffspring", {"start": v(53.03, -39.88) * mm, "end": v(71.92, -39.88) * mm});
            skLineSegment(sketch, "E401.trimOffspring", {"start": v(52.53, -44.86) * mm, "end": v(26.58, -44.86) * mm});
            skLineSegment(sketch, "E402.trimOffspring", {"start": v(71.92, -44.86) * mm, "end": v(53.03, -44.86) * mm});
            skLineSegment(sketch, "E403.trimOffspring", {"start": v(72.42, -39.88) * mm, "end": v(82.81, -39.88) * mm});
            skLineSegment(sketch, "E404.trimOffspring", {"start": v(40.2, -32.73) * mm, "end": v(59, -32.73) * mm});
            skLineSegment(sketch, "E405.trimOffspring", {"start": v(40.2, -39.38) * mm, "end": v(59, -39.38) * mm});
            skLineSegment(sketch, "E406.trimOffspring", {"start": v(26.58, -39.88) * mm, "end": v(52.53, -39.88) * mm});
            skLineSegment(sketch, "E407.trimOffspring", {"start": v(26.08, -44.86) * mm, "end": v(-4.66, -44.86) * mm});
            skLineSegment(sketch, "E408.trimOffspring", {"start": v(22.01, -32.23) * mm, "end": v(46.22, -32.23) * mm});
            skLineSegment(sketch, "E409.trimOffspring", {"start": v(15.53, -32.73) * mm, "end": v(39.7, -32.73) * mm});
            skLineSegment(sketch, "E410.trimOffspring", {"start": v(15.53, -39.38) * mm, "end": v(39.7, -39.38) * mm});
            skLineSegment(sketch, "E411.trimOffspring", {"start": v(-2.81, -32.23) * mm, "end": v(21.51, -32.23) * mm});
            skLineSegment(sketch, "E412.trimOffspring", {"start": v(-8.58, -32.73) * mm, "end": v(15.03, -32.73) * mm});
            skLineSegment(sketch, "E413.trimOffspring", {"start": v(-8.58, -39.38) * mm, "end": v(15.03, -39.38) * mm});
            skLineSegment(sketch, "E414.trimOffspring", {"start": v(-4.66, -39.88) * mm, "end": v(26.08, -39.88) * mm});
            skLineSegment(sketch, "E415.trimOffspring", {"start": v(-5.16, -44.86) * mm, "end": v(-30.77, -44.86) * mm});
            skLineSegment(sketch, "E416.trimOffspring", {"start": v(-21.66, -32.23) * mm, "end": v(-3.31, -32.23) * mm});
            skLineSegment(sketch, "E417.trimOffspring", {"start": v(-24.86, -32.73) * mm, "end": v(-9.08, -32.73) * mm});
            skLineSegment(sketch, "E418.trimOffspring", {"start": v(-24.86, -39.38) * mm, "end": v(-9.08, -39.38) * mm});
            skLineSegment(sketch, "E419.trimOffspring", {"start": v(-30.77, -39.88) * mm, "end": v(-5.16, -39.88) * mm});
            skLineSegment(sketch, "E420.trimOffspring", {"start": v(-31.27, -44.86) * mm, "end": v(-53.8, -44.86) * mm});
            skLineSegment(sketch, "E421.trimOffspring", {"start": v(-44.71, -32.23) * mm, "end": v(-22.16, -32.23) * mm});
            skLineSegment(sketch, "E422.trimOffspring", {"start": v(-46.18, -32.73) * mm, "end": v(-25.36, -32.73) * mm});
            skLineSegment(sketch, "E423.trimOffspring", {"start": v(-46.18, -39.38) * mm, "end": v(-25.36, -39.38) * mm});
            skLineSegment(sketch, "E424.trimOffspring", {"start": v(-53.8, -39.88) * mm, "end": v(-31.27, -39.88) * mm});
            skLineSegment(sketch, "E425.trimOffspring", {"start": v(-54.3, -44.86) * mm, "end": v(-64.64, -44.86) * mm});
            skLineSegment(sketch, "E426.trimOffspring", {"start": v(11.48, 10.97) * mm, "end": v(30.2, 10.97) * mm});
            skLineSegment(sketch, "E427.trimOffspring", {"start": v(30.7, 10.97) * mm, "end": v(82.81, 10.97) * mm});
            skLineSegment(sketch, "E428", {"start": v(11.48, 5.26) * mm, "end": v(30.2, 5.26) * mm});
            skLineSegment(sketch, "E429", {"start": v(-65.14, 34.42) * mm, "end": v(-65.14, 43.21) * mm});
            skLineSegment(sketch, "E430", {"start": v(-65.14, 43.21) * mm, "end": v(83.31, 43.21) * mm});
            skLineSegment(sketch, "E431", {"start": v(83.31, 34.42) * mm, "end": v(83.31, 43.21) * mm});
            skLineSegment(sketch, "E432.0", {"start": v(-64.64, 42.71) * mm, "end": v(-58.29, 42.71) * mm});
            skLineSegment(sketch, "E433", {"start": v(-65.97, 48.89) * mm, "end": v(-58.47, 48.89) * mm});
            skLineSegment(sketch, "E434", {"start": v(84.03, 56.8) * mm, "end": v(76.53, 56.8) * mm});
            skLineSegment(sketch, "E435", {"start": v(-65.97, 61.87) * mm, "end": v(-58.47, 61.87) * mm});
            skLineSegment(sketch, "E436.0", {"start": v(61.53, 68.57) * mm, "end": v(46.53, 68.57) * mm});
            skLineSegment(sketch, "E437.0", {"start": v(-65.97, 61.37) * mm, "end": v(-58.47, 61.37) * mm});
            skLineSegment(sketch, "E438.0", {"start": v(84.03, 57.3) * mm, "end": v(76.53, 57.3) * mm});
            skLineSegment(sketch, "E439.0", {"start": v(-65.97, 49.39) * mm, "end": v(-58.47, 49.39) * mm});
            skLineSegment(sketch, "E440", {"start": v(-58.47, 68.57) * mm, "end": v(-58.47, 48.89) * mm});
            skLineSegment(sketch, "E441", {"start": v(-65.97, 48.89) * mm, "end": v(-65.97, 49.39) * mm});
            skLineSegment(sketch, "E442", {"start": v(-28.47, 48.89) * mm, "end": v(-28.47, 49.39) * mm});
            skLineSegment(sketch, "E443", {"start": v(1.53, 48.87) * mm, "end": v(1.53, 48.89) * mm});
            skLineSegment(sketch, "E444", {"start": v(16.53, 68.57) * mm, "end": v(16.53, 68.07) * mm});
            skLineSegment(sketch, "E445", {"start": v(31.53, 48.87) * mm, "end": v(31.53, 49.39) * mm});
            skLineSegment(sketch, "E446", {"start": v(46.53, 68.57) * mm, "end": v(46.53, 68.07) * mm});
            skLineSegment(sketch, "E447.trimOffspring", {"start": v(84.03, 68.07) * mm, "end": v(84.03, 68.57) * mm});
            skLineSegment(sketch, "E448.trimOffspring", {"start": v(76.53, 61.87) * mm, "end": v(76.53, 61.37) * mm});
            skLineSegment(sketch, "E449.trimOffspring", {"start": v(76.53, 49.39) * mm, "end": v(76.53, 48.89) * mm});
            skLineSegment(sketch, "E450.trimOffspring", {"start": v(84.03, 56.8) * mm, "end": v(84.03, 61.87) * mm});
            skLineSegment(sketch, "E451.trimOffspring", {"start": v(76.53, 49.39) * mm, "end": v(84.03, 49.39) * mm});
            skLineSegment(sketch, "E452.trimOffspring", {"start": v(76.53, 48.89) * mm, "end": v(84.03, 48.89) * mm});
            skLineSegment(sketch, "E453.trimOffspring", {"start": v(76.53, 61.87) * mm, "end": v(84.03, 61.87) * mm});
            skLineSegment(sketch, "E454.trimOffspring", {"start": v(76.53, 61.37) * mm, "end": v(84.03, 61.37) * mm});
            skLineSegment(sketch, "E455.trimOffspring", {"start": v(61.53, 57.3) * mm, "end": v(46.53, 57.3) * mm});
            skLineSegment(sketch, "E456.trimOffspring", {"start": v(61.53, 56.8) * mm, "end": v(46.53, 56.8) * mm});
            skLineSegment(sketch, "E457.trimOffspring", {"start": v(61.53, 56.8) * mm, "end": v(61.53, 57.3) * mm});
            skLineSegment(sketch, "E458.trimOffspring", {"start": v(46.53, 49.39) * mm, "end": v(46.53, 48.89) * mm});
            skLineSegment(sketch, "E459.trimOffspring", {"start": v(46.53, 57.3) * mm, "end": v(46.53, 56.8) * mm});
            skLineSegment(sketch, "E460.trimOffspring", {"start": v(46.53, 61.87) * mm, "end": v(46.53, 61.37) * mm});
            skLineSegment(sketch, "E461.trimOffspring", {"start": v(31.53, 68.07) * mm, "end": v(31.53, 68.57) * mm});
            skLineSegment(sketch, "E462.trimOffspring", {"start": v(31.53, 61.37) * mm, "end": v(31.53, 61.87) * mm});
            skLineSegment(sketch, "E463.trimOffspring", {"start": v(31.53, 56.8) * mm, "end": v(31.53, 57.3) * mm});
            skLineSegment(sketch, "E464.trimOffspring", {"start": v(46.53, 48.89) * mm, "end": v(61.53, 48.89) * mm});
            skLineSegment(sketch, "E465.trimOffspring", {"start": v(46.53, 49.39) * mm, "end": v(61.53, 49.39) * mm});
            skLineSegment(sketch, "E466.trimOffspring", {"start": v(31.53, 56.8) * mm, "end": v(16.53, 56.8) * mm});
            skLineSegment(sketch, "E467.trimOffspring", {"start": v(46.53, 61.37) * mm, "end": v(61.53, 61.37) * mm});
            skLineSegment(sketch, "E468.trimOffspring", {"start": v(46.53, 61.87) * mm, "end": v(61.53, 61.87) * mm});
            skLineSegment(sketch, "E469.trimOffspring", {"start": v(1.53, 68.07) * mm, "end": v(1.53, 68.57) * mm});
            skLineSegment(sketch, "E470.trimOffspring", {"start": v(16.53, 57.3) * mm, "end": v(16.53, 56.8) * mm});
            skLineSegment(sketch, "E471.trimOffspring", {"start": v(1.53, 56.8) * mm, "end": v(1.53, 57.3) * mm});
            skLineSegment(sketch, "E472.trimOffspring", {"start": v(1.53, 61.37) * mm, "end": v(1.53, 61.87) * mm});
            skLineSegment(sketch, "E473.trimOffspring", {"start": v(16.53, 49.39) * mm, "end": v(16.53, 48.89) * mm});
            skLineSegment(sketch, "E474", {"start": v(1.53, 49.39) * mm, "end": v(1.53, 48.87) * mm});
            skLineSegment(sketch, "E475.trimOffspring", {"start": v(16.53, 49.39) * mm, "end": v(31.53, 49.39) * mm});
            skLineSegment(sketch, "E476.trimOffspring", {"start": v(16.53, 48.89) * mm, "end": v(31.53, 48.89) * mm});
            skLineSegment(sketch, "E477.trimOffspring", {"start": v(1.53, 56.8) * mm, "end": v(-13.47, 56.8) * mm});
            skLineSegment(sketch, "E478.trimOffspring", {"start": v(1.53, 57.3) * mm, "end": v(-13.47, 57.3) * mm});
            skLineSegment(sketch, "E479.trimOffspring", {"start": v(1.53, 68.57) * mm, "end": v(-13.47, 68.57) * mm});
            skLineSegment(sketch, "E480.trimOffspring", {"start": v(1.53, 68.07) * mm, "end": v(-13.47, 68.07) * mm});
            skLineSegment(sketch, "E481", {"start": v(31.53, 57.3) * mm, "end": v(16.53, 57.3) * mm});
            skLineSegment(sketch, "E482", {"start": v(31.53, 61.37) * mm, "end": v(16.53, 61.37) * mm});
            skLineSegment(sketch, "E483", {"start": v(16.5, 68.57) * mm, "end": v(16.53, 68.07) * mm});
            skLineSegment(sketch, "E484", {"start": v(31.53, 61.87) * mm, "end": v(16.53, 61.87) * mm});
            skLineSegment(sketch, "E485", {"start": v(16.53, 61.87) * mm, "end": v(16.53, 61.37) * mm});
            skLineSegment(sketch, "E486", {"start": v(16.53, 68.07) * mm, "end": v(31.53, 68.07) * mm});
            skLineSegment(sketch, "E487", {"start": v(31.53, 68.57) * mm, "end": v(16.53, 68.57) * mm});
            skLineSegment(sketch, "E488", {"start": v(-13.47, 61.87) * mm, "end": v(-13.47, 61.37) * mm});
            skLineSegment(sketch, "E489", {"start": v(-13.47, 61.37) * mm, "end": v(1.53, 61.37) * mm});
            skLineSegment(sketch, "E490", {"start": v(-13.47, 56.8) * mm, "end": v(-13.47, 57.3) * mm});
            skLineSegment(sketch, "E491", {"start": v(-13.47, 68.57) * mm, "end": v(-13.47, 68.07) * mm});
            skLineSegment(sketch, "E492", {"start": v(-13.47, 49.39) * mm, "end": v(-13.47, 48.89) * mm});
            skLineSegment(sketch, "E493.trimOffspring", {"start": v(-28.47, 68.57) * mm, "end": v(-43.47, 68.57) * mm});
            skLineSegment(sketch, "E494.trimOffspring", {"start": v(-28.47, 68.07) * mm, "end": v(-43.47, 68.07) * mm});
            skLineSegment(sketch, "E495.trimOffspring", {"start": v(-13.47, 61.87) * mm, "end": v(1.53, 61.87) * mm});
            skLineSegment(sketch, "E496.trimOffspring", {"start": v(-28.47, 57.3) * mm, "end": v(-43.47, 57.3) * mm});
            skLineSegment(sketch, "E497.trimOffspring", {"start": v(-28.47, 56.8) * mm, "end": v(-43.47, 56.8) * mm});
            skLineSegment(sketch, "E498.trimOffspring", {"start": v(-13.47, 49.39) * mm, "end": v(1.53, 49.39) * mm});
            skLineSegment(sketch, "E499.trimOffspring", {"start": v(-43.47, 48.89) * mm, "end": v(-28.47, 48.89) * mm});
            skLineSegment(sketch, "E500.trimOffspring", {"start": v(-43.47, 49.39) * mm, "end": v(-28.47, 49.39) * mm});
            skLineSegment(sketch, "E501.trimOffspring", {"start": v(-58.47, 56.8) * mm, "end": v(-65.97, 56.8) * mm});
            skLineSegment(sketch, "E502.trimOffspring", {"start": v(-58.47, 57.3) * mm, "end": v(-65.97, 57.3) * mm});
            skLineSegment(sketch, "E503.trimOffspring", {"start": v(-43.47, 61.37) * mm, "end": v(-28.47, 61.37) * mm});
            skLineSegment(sketch, "E504.trimOffspring", {"start": v(-43.47, 61.87) * mm, "end": v(-28.47, 61.87) * mm});
            skLineSegment(sketch, "E505.trimOffspring", {"start": v(-58.47, 68.07) * mm, "end": v(-65.97, 68.07) * mm});
            skLineSegment(sketch, "E506.trimOffspring", {"start": v(-58.47, 68.57) * mm, "end": v(-65.97, 68.57) * mm});
            skLineSegment(sketch, "E507.trimOffspring", {"start": v(-65.97, 68.07) * mm, "end": v(-65.97, 68.57) * mm});
            skLineSegment(sketch, "E508.trimOffspring", {"start": v(-65.97, 61.37) * mm, "end": v(-65.97, 61.87) * mm});
            skLineSegment(sketch, "E509.trimOffspring", {"start": v(-65.97, 56.8) * mm, "end": v(-65.97, 57.3) * mm});
            skLineSegment(sketch, "E510.trimOffspring", {"start": v(-43.47, 49.39) * mm, "end": v(-43.47, 48.89) * mm});
            skLineSegment(sketch, "E511.trimOffspring", {"start": v(-43.47, 57.3) * mm, "end": v(-43.47, 56.8) * mm});
            skLineSegment(sketch, "E512.trimOffspring", {"start": v(-43.47, 61.87) * mm, "end": v(-43.47, 61.37) * mm});
            skLineSegment(sketch, "E513.trimOffspring", {"start": v(-28.47, 68.07) * mm, "end": v(-28.47, 68.57) * mm});
            skLineSegment(sketch, "E514.trimOffspring", {"start": v(-28.47, 61.37) * mm, "end": v(-28.47, 61.87) * mm});
            skLineSegment(sketch, "E515.trimOffspring", {"start": v(-28.47, 56.8) * mm, "end": v(-28.47, 57.3) * mm});
            skLineSegment(sketch, "E516.trimOffspring", {"start": v(-13.47, 57.3) * mm, "end": v(-13.47, 56.8) * mm});
            skLineSegment(sketch, "E517.trimOffspring", {"start": v(61.53, 61.37) * mm, "end": v(61.53, 61.87) * mm});
            skLineSegment(sketch, "E518.trimOffspring", {"start": v(76.53, 57.3) * mm, "end": v(76.53, 56.8) * mm});
            skLineSegment(sketch, "E519", {"start": v(46.53, 68.07) * mm, "end": v(61.53, 68.07) * mm});
            skLineSegment(sketch, "E520", {"start": v(61.53, 68.07) * mm, "end": v(61.53, 68.57) * mm});
            skLineSegment(sketch, "E521", {"start": v(84.03, 68.07) * mm, "end": v(76.53, 68.07) * mm});
            skLineSegment(sketch, "E522", {"start": v(84.03, 68.57) * mm, "end": v(76.53, 68.57) * mm});
            skLineSegment(sketch, "E523", {"start": v(76.53, 68.57) * mm, "end": v(76.53, 68.07) * mm});
            skLineSegment(sketch, "E524", {"start": v(-43.47, 68.57) * mm, "end": v(-43.47, 68.07) * mm});
            skLineSegment(sketch, "E525", {"start": v(-13.47, 48.89) * mm, "end": v(1.53, 48.89) * mm});
            skLineSegment(sketch, "E526", {"start": v(46.53, 48.89) * mm, "end": v(46.53, 49.39) * mm});
            skLineSegment(sketch, "E527", {"start": v(61.53, 49.39) * mm, "end": v(61.53, 48.89) * mm});
            skLineSegment(sketch, "E528", {"start": v(84.03, 48.89) * mm, "end": v(84.03, 49.39) * mm});
            skLineSegment(sketch, "E529", {"start": v(-58.29, 34.42) * mm, "end": v(-58.29, 42.71) * mm});
            skLineSegment(sketch, "E530", {"start": v(-47.35, 34.42) * mm, "end": v(-47.35, 42.71) * mm});
            skLineSegment(sketch, "E531", {"start": v(-28.92, 34.42) * mm, "end": v(-28.92, 42.71) * mm});
            skLineSegment(sketch, "E532", {"start": v(-12.94, 34.42) * mm, "end": v(-12.94, 42.71) * mm});
            skLineSegment(sketch, "E533", {"start": v(10.23, 42.71) * mm, "end": v(10.23, 34.42) * mm});
            skLineSegment(sketch, "E534", {"start": v(29.46, 34.42) * mm, "end": v(29.46, 42.71) * mm});
            skLineSegment(sketch, "E535", {"start": v(47.37, 34.42) * mm, "end": v(47.37, 42.71) * mm});
            skLineSegment(sketch, "E536", {"start": v(61, 42.71) * mm, "end": v(61, 34.42) * mm});
            skLineSegment(sketch, "E537", {"start": v(75.32, 34.42) * mm, "end": v(75.32, 42.71) * mm});
            skLineSegment(sketch, "E538.0", {"start": v(75.82, 34.42) * mm, "end": v(75.82, 42.71) * mm});
            skLineSegment(sketch, "E539.0", {"start": v(60.5, 42.71) * mm, "end": v(60.5, 34.42) * mm});
            skLineSegment(sketch, "E540.0", {"start": v(47.87, 34.42) * mm, "end": v(47.87, 42.71) * mm});
            skLineSegment(sketch, "E541.0", {"start": v(29.96, 34.42) * mm, "end": v(29.96, 42.71) * mm});
            skLineSegment(sketch, "E542.0", {"start": v(9.73, 42.71) * mm, "end": v(9.73, 34.42) * mm});
            skLineSegment(sketch, "E543.0", {"start": v(-12.44, 34.42) * mm, "end": v(-12.44, 42.71) * mm});
            skLineSegment(sketch, "E544.0", {"start": v(-28.42, 34.42) * mm, "end": v(-28.42, 42.71) * mm});
            skLineSegment(sketch, "E545.0", {"start": v(-46.85, 34.42) * mm, "end": v(-46.85, 42.71) * mm});
            skLineSegment(sketch, "E546.0", {"start": v(-57.79, 34.42) * mm, "end": v(-57.79, 42.71) * mm});
            skLineSegment(sketch, "E547.0", {"start": v(-64.64, 34.42) * mm, "end": v(-64.64, 42.71) * mm});
            skLineSegment(sketch, "E548.0", {"start": v(82.81, 34.42) * mm, "end": v(82.81, 42.71) * mm});
            skLineSegment(sketch, "E549.trimOffspring", {"start": v(75.82, 34.42) * mm, "end": v(82.81, 34.42) * mm});
            skLineSegment(sketch, "E550.trimOffspring", {"start": v(75.82, 42.71) * mm, "end": v(82.81, 42.71) * mm});
            skLineSegment(sketch, "E551.trimOffspring", {"start": v(61, 42.71) * mm, "end": v(75.32, 42.71) * mm});
            skLineSegment(sketch, "E552.trimOffspring", {"start": v(61, 34.42) * mm, "end": v(75.32, 34.42) * mm});
            skLineSegment(sketch, "E553.trimOffspring", {"start": v(47.87, 42.71) * mm, "end": v(60.5, 42.71) * mm});
            skLineSegment(sketch, "E554.trimOffspring", {"start": v(47.87, 34.42) * mm, "end": v(60.5, 34.42) * mm});
            skLineSegment(sketch, "E555.trimOffspring", {"start": v(29.96, 34.42) * mm, "end": v(47.37, 34.42) * mm});
            skLineSegment(sketch, "E556.trimOffspring", {"start": v(29.96, 42.71) * mm, "end": v(47.37, 42.71) * mm});
            skLineSegment(sketch, "E557.trimOffspring", {"start": v(10.23, 42.71) * mm, "end": v(29.46, 42.71) * mm});
            skLineSegment(sketch, "E558.trimOffspring", {"start": v(10.23, 34.42) * mm, "end": v(29.46, 34.42) * mm});
            skLineSegment(sketch, "E559.trimOffspring", {"start": v(-12.44, 34.42) * mm, "end": v(9.73, 34.42) * mm});
            skLineSegment(sketch, "E560.trimOffspring", {"start": v(-12.44, 42.71) * mm, "end": v(9.73, 42.71) * mm});
            skLineSegment(sketch, "E561.trimOffspring", {"start": v(-28.42, 34.42) * mm, "end": v(-12.94, 34.42) * mm});
            skLineSegment(sketch, "E562.trimOffspring", {"start": v(-28.42, 42.71) * mm, "end": v(-12.94, 42.71) * mm});
            skLineSegment(sketch, "E563.trimOffspring", {"start": v(-46.85, 42.71) * mm, "end": v(-28.92, 42.71) * mm});
            skLineSegment(sketch, "E564.trimOffspring", {"start": v(-46.85, 34.42) * mm, "end": v(-28.92, 34.42) * mm});
            skLineSegment(sketch, "E565.trimOffspring", {"start": v(-57.79, 34.42) * mm, "end": v(-47.35, 34.42) * mm});
            skLineSegment(sketch, "E566.trimOffspring", {"start": v(-57.79, 42.71) * mm, "end": v(-47.35, 42.71) * mm});
            skSolve(sketch);
        }
        {
            var Q0;
            Q0=qSketchRegion(id+"F2",true);
            extrude(context, id + "F3", {"entities" : qUnion([Q0]), "operationType" : NewBodyOperationType.REMOVE, "oppositeDirection" : true, "depth" : 0.5 * mm, "offsetDistance" : 25 * mm});
        }
        {
            var Q0;
            Q0=makeQuery(id+"F1.opExtrude","CAP_FACE",FACE,{"disambiguationData":[OSD([sQuery(id+"F0.wireOp",EDGE,"E0.bottom"),sQuery(id+"F0.wireOp",EDGE,"E0.top"),sQuery(id+"F0.wireOp",EDGE,"E0.left"),sQuery(id+"F0.wireOp",EDGE,"E0.right"),sQuery(id+"F0.wireOp",EDGE,"E1"),sQuery(id+"F0.wireOp",EDGE,"E2"),sQuery(id+"F0.wireOp",EDGE,"E3"),sQuery(id+"F0.wireOp",EDGE,"E5"),sQuery(id+"F0.wireOp",EDGE,"E6"),sQuery(id+"F0.wireOp",EDGE,"E7"),sQuery(id+"F0.wireOp",EDGE,"E9"),sQuery(id+"F0.wireOp",EDGE,"E10"),sQuery(id+"F0.wireOp",EDGE,"E11"),sQuery(id+"F0.wireOp",EDGE,"E4"),sQuery(id+"F0.wireOp",EDGE,"E8"),sQuery(id+"F0.wireOp",EDGE,"E12.trimOffspring"),sQuery(id+"F0.wireOp",EDGE,"E13"),sQuery(id+"F0.wireOp",EDGE,"E14"),sQuery(id+"F0.wireOp",EDGE,"E15"),sQuery(id+"F0.wireOp",EDGE,"E16"),sQuery(id+"F0.wireOp",EDGE,"E17"),sQuery(id+"F0.wireOp",EDGE,"E18"),sQuery(id+"F0.wireOp",EDGE,"E19.trimOffspring"),sQuery(id+"F0.wireOp",EDGE,"E20.trimOffspring")])],"isStart":true});
            var sketch = newSketch(context, id + "F4", { "sketchPlane" : qUnion([Q0])});
            skLineSegment(sketch, "E567", {"start": v(-69.03, -46.19) * mm, "end": v(-69.03, 33.81) * mm});
            skLineSegment(sketch, "E568", {"start": v(-69.03, 33.81) * mm, "end": v(-59.03, 33.81) * mm});
            skLineSegment(sketch, "E569", {"start": v(-59.03, 33.81) * mm, "end": v(-59.03, -46.19) * mm});
            skLineSegment(sketch, "E570", {"start": v(-59.03, -46.19) * mm, "end": v(-69.03, -46.19) * mm});
            skLineSegment(sketch, "E571", {"start": v(-15.4, -46.19) * mm, "end": v(-15.4, 33.81) * mm});
            skLineSegment(sketch, "E572", {"start": v(-15.4, 33.81) * mm, "end": v(-5.4, 33.81) * mm});
            skLineSegment(sketch, "E573", {"start": v(-5.4, 33.81) * mm, "end": v(-5.4, -46.19) * mm});
            skLineSegment(sketch, "E574", {"start": v(-5.4, -46.19) * mm, "end": v(-15.4, -46.19) * mm});
            skLineSegment(sketch, "E575", {"start": v(40.97, -46.19) * mm, "end": v(40.97, 33.81) * mm});
            skLineSegment(sketch, "E576", {"start": v(40.97, 33.81) * mm, "end": v(50.97, 33.81) * mm});
            skLineSegment(sketch, "E577", {"start": v(50.97, 33.81) * mm, "end": v(50.97, -46.19) * mm});
            skLineSegment(sketch, "E578", {"start": v(50.97, -46.19) * mm, "end": v(40.97, -46.19) * mm});
            skSolve(sketch);
        }
        {
            var Q0;
            Q0=qSketchRegion(id+"F4",true);
            extrude(context, id + "F5", {"entities" : qUnion([Q0]), "operationType" : NewBodyOperationType.ADD, "depth" : 10 * mm, "offsetDistance" : 25 * mm});
        }
        {
            var Q0;
            Q0=makeQuery(id+"F1.opExtrude","CAP_FACE",FACE,{"disambiguationData":[OSD([sQuery(id+"F0.wireOp",EDGE,"E0.bottom"),sQuery(id+"F0.wireOp",EDGE,"E0.top"),sQuery(id+"F0.wireOp",EDGE,"E0.left"),sQuery(id+"F0.wireOp",EDGE,"E0.right"),sQuery(id+"F0.wireOp",EDGE,"E1"),sQuery(id+"F0.wireOp",EDGE,"E2"),sQuery(id+"F0.wireOp",EDGE,"E3"),sQuery(id+"F0.wireOp",EDGE,"E5"),sQuery(id+"F0.wireOp",EDGE,"E6"),sQuery(id+"F0.wireOp",EDGE,"E7"),sQuery(id+"F0.wireOp",EDGE,"E9"),sQuery(id+"F0.wireOp",EDGE,"E10"),sQuery(id+"F0.wireOp",EDGE,"E11"),sQuery(id+"F0.wireOp",EDGE,"E4"),sQuery(id+"F0.wireOp",EDGE,"E8"),sQuery(id+"F0.wireOp",EDGE,"E12.trimOffspring"),sQuery(id+"F0.wireOp",EDGE,"E13"),sQuery(id+"F0.wireOp",EDGE,"E14"),sQuery(id+"F0.wireOp",EDGE,"E15"),sQuery(id+"F0.wireOp",EDGE,"E16"),sQuery(id+"F0.wireOp",EDGE,"E17"),sQuery(id+"F0.wireOp",EDGE,"E18"),sQuery(id+"F0.wireOp",EDGE,"E19.trimOffspring"),sQuery(id+"F0.wireOp",EDGE,"E20.trimOffspring")])],"isStart":true});
            var sketch = newSketch(context, id + "F6", { "sketchPlane" : qUnion([Q0])});
            skLineSegment(sketch, "E579", {"start": v(-80.02, 38.81) * mm, "end": v(65.97, 38.81) * mm});
            skLineSegment(sketch, "E580", {"start": v(65.97, 38.81) * mm, "end": v(65.97, 73.81) * mm});
            skLineSegment(sketch, "E581", {"start": v(65.97, 73.81) * mm, "end": v(-84.03, 73.81) * mm});
            skLineSegment(sketch, "E582", {"start": v(-84.03, 73.81) * mm, "end": v(-84.03, 38.81) * mm});
            skLineSegment(sketch, "E583", {"start": v(-80.02, 38.81) * mm, "end": v(-84.03, 38.81) * mm});
            skSolve(sketch);
        }
        {
            var Q0;
            Q0 = qSketchRegion(id + "F6", true);
            extrude(context, id + "F7", {"entities" : qUnion([Q0]), "operationType" : NewBodyOperationType.REMOVE, "oppositeDirection" : true, "depth" : 25 * mm, "offsetDistance" : 25 * mm});
        }
    });
